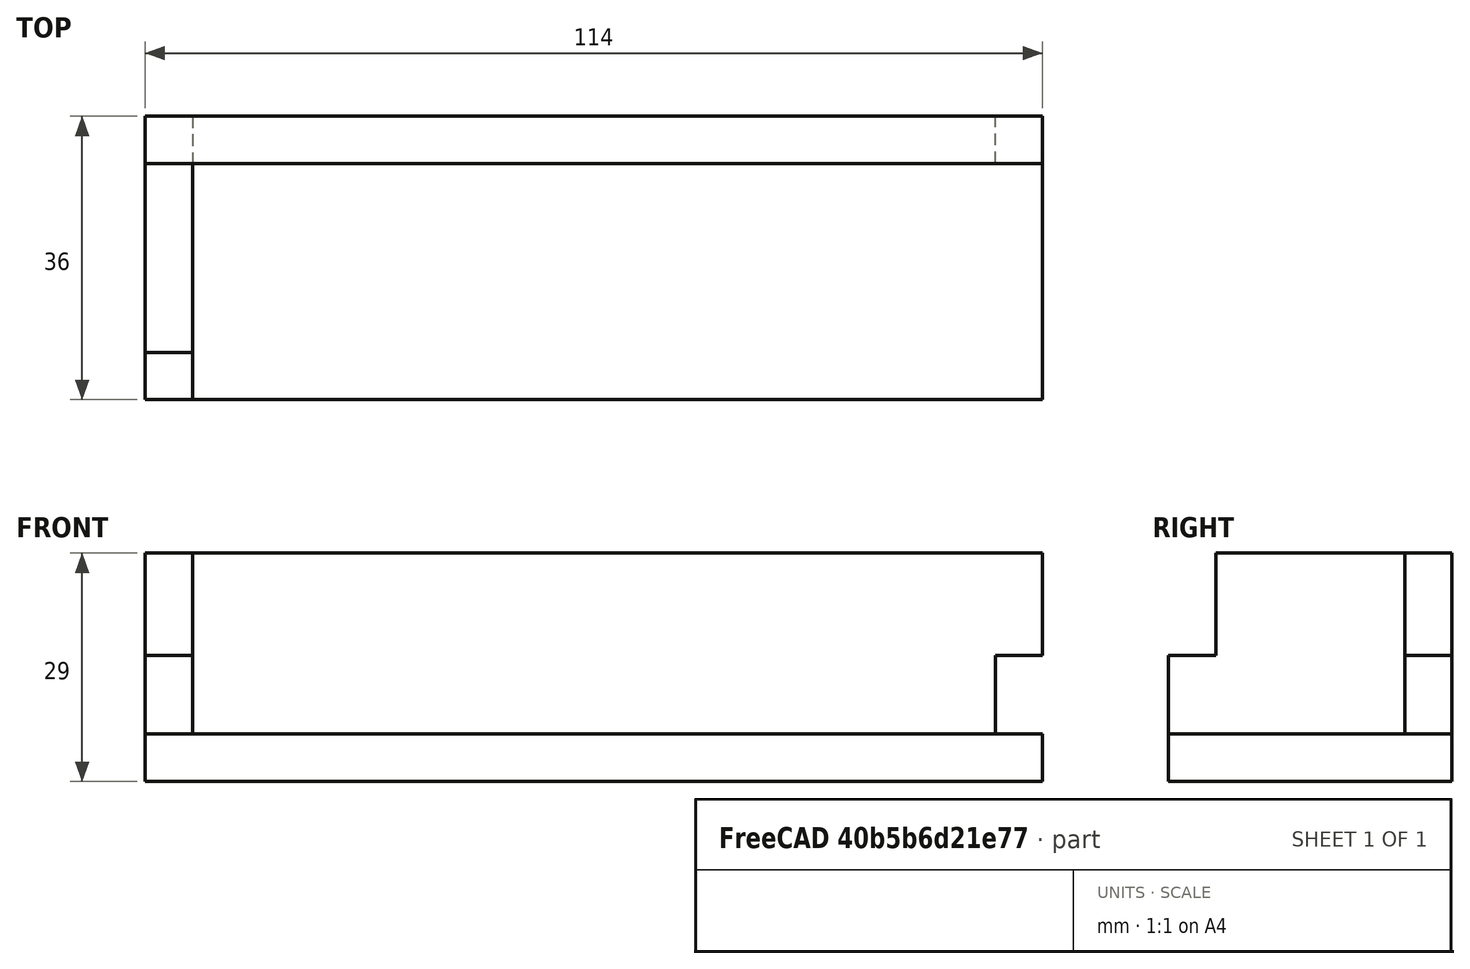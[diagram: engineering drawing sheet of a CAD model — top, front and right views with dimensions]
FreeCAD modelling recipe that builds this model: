
FCSTD DOCUMENT  (FreeCAD 0.18R16146 (Git))
Label: brass birmingham - resource tray
License: All rights reserved
LicenseURL: http://en.wikipedia.org/wiki/All_rights_reserved
objects: TechDraw::DrawViewPart×7, Sketcher::SketchObject×5, PartDesign::Body×5, PartDesign::Pad×3, Spreadsheet::Sheet×2, PartDesign::Pocket×2, PartDesign::FeatureBase×2, App::DocumentObjectGroup×2, TechDraw::DrawSVGTemplate×2, TechDraw::DrawViewDimension×2, TechDraw::DrawPage×2
note: 22 computed .brp shape members not serialized (recipe doc carries the construction recipe); baked Part::Feature solids carry a one-line shape summary decoded from their .brp

FEATURE [Spreadsheet::Sheet] Spreadsheet  label="my_variables"
  cells = A1=foam_width; B1(foam_width)==6mm; A2=lower_height; B2(lower_height)==29mm; A3=outer height (minus base); B3(height_adjusted)==38mm - B1; A4=outer long width; B4(width_long)==96mm; A5=outer short width; B5(width_short)==59mm
FEATURE [Sketcher::SketchObject] Sketch
  MapMode = 5
  Support = -> [XY_Plane]
  expr: Constraints[9] = my_variables001.width_short
  expr: Constraints[10] = my_variables001.width_long
  sketch-geometry (4):
    g0: LineSegment StartX=-57 StartY=36 StartZ=0 EndX=57 EndY=36 EndZ=0
    g1: LineSegment StartX=57 StartY=36 StartZ=0 EndX=57 EndY=0 EndZ=0
    g2: LineSegment StartX=57 StartY=0 StartZ=0 EndX=-57 EndY=0 EndZ=0
    g3: LineSegment StartX=-57 StartY=0 StartZ=0 EndX=-57 EndY=36 EndZ=0
  constraints (11):
    c: Coincident(g0,g1)
    c: Coincident(g1,g2)
    c: Coincident(g2,g3)
    c: Coincident(g3,g0)
    c: Horizontal(g0)
    c: Horizontal(g2)
    c: Vertical(g1)
    c: Vertical(g3)
    c: Symmetric(g2,g2,g-1)
    c: Distance(g3) = 36
    c: Distance(g2) = 114
FEATURE [PartDesign::Pad] Pad
  Length = 6
  Length2 = 100
  Profile = -> Sketch
  Type = 0
  expr: Length = my_variables.foam_width
FEATURE [PartDesign::Body] Body  label="base"
  Group = -> [Sketch,Pad]
  Origin = -> Origin
  Tip = -> Pad
FEATURE [Sketcher::SketchObject] Sketch001
  MapMode = 5
  Placement = pos=(0,0,0) rot=(1,0,0;1.5708rad)
  Support = -> [XZ_Plane001]
  expr: Constraints[10] = my_variables001.width_long
  expr: Constraints[9] = my_variables001.height_adjusted
  sketch-geometry (4):
    g0: LineSegment StartX=-57 StartY=23 StartZ=0 EndX=57 EndY=23 EndZ=0
    g1: LineSegment StartX=57 StartY=23 StartZ=0 EndX=57 EndY=0 EndZ=0
    g2: LineSegment StartX=57 StartY=0 StartZ=0 EndX=-57 EndY=0 EndZ=0
    g3: LineSegment StartX=-57 StartY=0 StartZ=0 EndX=-57 EndY=23 EndZ=0
  constraints (11):
    c: Coincident(g0,g1)
    c: Coincident(g1,g2)
    c: Coincident(g2,g3)
    c: Coincident(g3,g0)
    c: Horizontal(g0)
    c: Horizontal(g2)
    c: Vertical(g1)
    c: Vertical(g3)
    c: Symmetric(g2,g2,g-1)
    c: Distance(g3) = 23
    c: Distance(g0) = 114
FEATURE [PartDesign::Pad] Pad001
  Length = 6
  Length2 = 100
  Placement = pos=(0,0,0) rot=(1,0,0;1.5708rad)
  Profile = -> Sketch001
  Type = 0
  expr: Length = my_variables.foam_width
FEATURE [Sketcher::SketchObject] Sketch002
  MapMode = 5
  Placement = pos=(0,-6,-1.3e-15) rot=(1,0,0;1.5708rad)
  Support = -> [Pad001]
  expr: Constraints[30] = my_variables.foam_width
  expr: Constraints[29] = my_variables.foam_width
  expr: Constraints[10] = Sketch001.Constraints[10]
  expr: Constraints[9] = Sketch001.Constraints[9]
  sketch-geometry (12):
    g0: LineSegment [constr] StartX=-57 StartY=23 StartZ=0 EndX=57 EndY=23 EndZ=0
    g1: LineSegment [constr] StartX=57 StartY=23 StartZ=0 EndX=57 EndY=0 EndZ=0
    g2: LineSegment [constr] StartX=57 StartY=0 StartZ=0 EndX=-57 EndY=0 EndZ=0
    g3: LineSegment [constr] StartX=-57 StartY=0 StartZ=0 EndX=-57 EndY=23 EndZ=0
    g4: LineSegment StartX=-57 StartY=10 StartZ=0 EndX=-51 EndY=10 EndZ=0
    g5: LineSegment StartX=-51 StartY=10 StartZ=0 EndX=-51 EndY=0 EndZ=0
    g6: LineSegment StartX=-51 StartY=0 StartZ=0 EndX=-57 EndY=0 EndZ=0
    g7: LineSegment StartX=-57 StartY=0 StartZ=0 EndX=-57 EndY=10 EndZ=0
    g8: LineSegment StartX=51 StartY=10 StartZ=0 EndX=57 EndY=10 EndZ=0
    g9: LineSegment StartX=57 StartY=10 StartZ=0 EndX=57 EndY=0 EndZ=0
    g10: LineSegment StartX=57 StartY=0 StartZ=0 EndX=51 EndY=0 EndZ=0
    g11: LineSegment StartX=51 StartY=0 StartZ=0 EndX=51 EndY=10 EndZ=0
  constraints (33):
    c: Coincident(g0,g1)
    c: Coincident(g1,g2)
    c: Coincident(g2,g3)
    c: Coincident(g3,g0)
    c: Horizontal(g0)
    c: Horizontal(g2)
    c: Vertical(g1)
    c: Vertical(g3)
    c: Symmetric(g2,g2,g-1)
    c: Distance(g3) = 23
    c: Distance(g0) = 114
    c: Coincident(g4,g5)
    c: Coincident(g5,g6)
    c: Coincident(g6,g7)
    c: Coincident(g7,g4)
    c: Horizontal(g4)
    c: Horizontal(g6)
    c: Vertical(g5)
    c: Vertical(g7)
    c: Coincident(g8,g9)
    c: Coincident(g9,g10)
    c: Coincident(g10,g11)
    c: Coincident(g11,g8)
    c: Horizontal(g8)
    c: Horizontal(g10)
    c: Vertical(g9)
    c: Vertical(g11)
    c: Coincident(g6,g2)
    c: Coincident(g9,g1)
    c: Distance(g4) = 6
    c: Distance(g8) = 6
    c: Distance(g5) = 10
    c: Distance(g11) = 10
FEATURE [PartDesign::Pocket] Pocket
  BaseFeature = -> Pad001
  Length = 5
  Length2 = 100
  Placement = pos=(0,0,0) rot=(1,0,0;1.5708rad)
  Profile = -> Sketch002
  Type = 1
FEATURE [PartDesign::Body] Body001  label="side long"
  Group = -> [Sketch001,Pad001,Sketch002,Pocket]
  Origin = -> Origin001
  Placement = pos=(7e-15,6,6) rot=(0,0,1;0rad)
  Tip = -> Pocket
FEATURE [PartDesign::FeatureBase] Clone
  BaseFeature = -> Body001
  Placement = pos=(7e-15,6,6) rot=(0,0,1;0rad)
FEATURE [PartDesign::Body] Body002  label="side long - clone"
  BaseFeature = -> Body001
  Group = -> [Clone]
  Origin = -> Origin002
  Placement = pos=(-1.4e-14,30,-1.1e-14) rot=(0,0,1;0rad)
  Tip = -> Clone
FEATURE [Sketcher::SketchObject] Sketch003
  MapMode = 5
  Placement = pos=(0,0,0) rot=(0.57735,0.57735,0.57735;2.0944rad)
  Support = -> [YZ_Plane003]
  expr: Constraints[10] = my_variables001.width_short
  expr: Constraints[9] = my_variables001.height_adjusted
  sketch-geometry (4):
    g0: LineSegment StartX=-18 StartY=23 StartZ=0 EndX=18 EndY=23 EndZ=0
    g1: LineSegment StartX=18 StartY=23 StartZ=0 EndX=18 EndY=0 EndZ=0
    g2: LineSegment StartX=18 StartY=0 StartZ=0 EndX=-18 EndY=0 EndZ=0
    g3: LineSegment StartX=-18 StartY=0 StartZ=0 EndX=-18 EndY=23 EndZ=0
  constraints (11):
    c: Coincident(g0,g1)
    c: Coincident(g1,g2)
    c: Coincident(g2,g3)
    c: Coincident(g3,g0)
    c: Horizontal(g0)
    c: Horizontal(g2)
    c: Vertical(g1)
    c: Vertical(g3)
    c: Symmetric(g2,g2,g-1)
    c: Distance(g3) = 23
    c: Distance(g0) = 36
FEATURE [PartDesign::Pad] Pad002
  Length = 6
  Length2 = 100
  Placement = pos=(0,0,0) rot=(0.57735,0.57735,0.57735;2.0944rad)
  Profile = -> Sketch003
  Type = 0
  expr: Length = my_variables.foam_width
FEATURE [Sketcher::SketchObject] Sketch004
  MapMode = 5
  Placement = pos=(6,-2.7e-15,2e-15) rot=(0.57735,0.57735,0.57735;2.0944rad)
  Support = -> [Pad002]
  expr: Constraints[31] = my_variables001.foam_width
  expr: Constraints[20] = my_variables001.foam_width
  expr: Constraints[9] = Sketch003.Constraints[9]
  expr: Constraints[10] = Sketch003.Constraints[10]
  sketch-geometry (12):
    g0: LineSegment [constr] StartX=-18 StartY=23 StartZ=0 EndX=18 EndY=23 EndZ=0
    g1: LineSegment [constr] StartX=18 StartY=23 StartZ=0 EndX=18 EndY=0 EndZ=0
    g2: LineSegment [constr] StartX=18 StartY=0 StartZ=0 EndX=-18 EndY=0 EndZ=0
    g3: LineSegment [constr] StartX=-18 StartY=0 StartZ=0 EndX=-18 EndY=23 EndZ=0
    g4: LineSegment StartX=12 StartY=23 StartZ=0 EndX=18 EndY=23 EndZ=0
    g5: LineSegment StartX=18 StartY=23 StartZ=0 EndX=18 EndY=10 EndZ=0
    g6: LineSegment StartX=18 StartY=10 StartZ=0 EndX=12 EndY=10 EndZ=0
    g7: LineSegment StartX=12 StartY=10 StartZ=0 EndX=12 EndY=23 EndZ=0
    g8: LineSegment StartX=-12 StartY=10 StartZ=0 EndX=-18 EndY=10 EndZ=0
    g9: LineSegment StartX=-18 StartY=10 StartZ=0 EndX=-18 EndY=23 EndZ=0
    g10: LineSegment StartX=-18 StartY=23 StartZ=0 EndX=-12 EndY=23 EndZ=0
    g11: LineSegment StartX=-12 StartY=23 StartZ=0 EndX=-12 EndY=10 EndZ=0
  constraints (33):
    c: Coincident(g0,g1)
    c: Coincident(g1,g2)
    c: Coincident(g2,g3)
    c: Coincident(g3,g0)
    c: Horizontal(g0)
    c: Horizontal(g2)
    c: Vertical(g1)
    c: Vertical(g3)
    c: Symmetric(g2,g2,g-1)
    c: Distance(g3) = 23
    c: Distance(g0) = 36
    c: Coincident(g4,g5)
    c: Coincident(g5,g6)
    c: Coincident(g6,g7)
    c: Coincident(g7,g4)
    c: Horizontal(g4)
    c: Horizontal(g6)
    c: Vertical(g5)
    c: Vertical(g7)
    c: Coincident(g4,g0)
    c: Distance(g6) = 6
    c: Distance(g5,g1) = 10
    c: Coincident(g8,g9)
    c: Coincident(g9,g10)
    c: Coincident(g10,g11)
    c: Coincident(g11,g8)
    c: Horizontal(g8)
    c: Horizontal(g10)
    c: Vertical(g9)
    c: Vertical(g11)
    c: Coincident(g9,g0)
    c: Distance(g8) = 6
    c: Distance(g8,g2) = 10
FEATURE [PartDesign::Pocket] Pocket001
  BaseFeature = -> Pad002
  Length = 5
  Length2 = 100
  Placement = pos=(0,0,0) rot=(0.57735,0.57735,0.57735;2.0944rad)
  Profile = -> Sketch004
  Type = 1
FEATURE [PartDesign::Body] Body003  label="side short"
  Group = -> [Sketch003,Pad002,Sketch004,Pocket001]
  Origin = -> Origin003
  Placement = pos=(51,18,6) rot=(0,0,1;0rad)
  Tip = -> Pocket001
FEATURE [App::DocumentObjectGroup] Group  label="parts"
  Group = -> [Body,Body001,Body003]
FEATURE [PartDesign::FeatureBase] Clone001
  BaseFeature = -> Body003
  Placement = pos=(34,25,6) rot=(0,0,1;0rad)
FEATURE [PartDesign::Body] Body004  label="side small - clone"
  BaseFeature = -> Body003
  Group = -> [Clone001]
  Origin = -> Origin004
  Placement = pos=(-91,-7,-2e-16) rot=(0,0,1;0rad)
  Tip = -> Clone001
FEATURE [App::DocumentObjectGroup] Group001  label="clones"
  Group = -> [Body002,Body004]
FEATURE [TechDraw::DrawSVGTemplate] Template
  Height = 210
  Orientation = 1
  Width = 297
FEATURE [TechDraw::DrawViewPart] View002
  CoarseView = false
  Direction = (0,0,1)
  Focus = 100
  HardHidden = false
  IsoCount = 0
  IsoHidden = false
  IsoVisible = false
  LockPosition = false
  Perspective = false
  Rotation = 0
  ScaleType = 0
  SeamHidden = false
  SeamVisible = false
  SmoothHidden = false
  SmoothVisible = false
  Source = -> [Body]
  X = 62.9845
  Y = 172.655
FEATURE [TechDraw::DrawViewDimension] Dimension
  Arbitrary = false
  FormatSpec = %.2f
  LockPosition = false
  MeasureType = 1
  OverTolerance = 0
  References2D = -> [View002]
  Rotation = 0
  ScaleType = 0
  Type = 0
  UnderTolerance = 0
  X = -58.2835
  Y = 2.70619
FEATURE [TechDraw::DrawViewDimension] Dimension001
  Arbitrary = false
  FormatSpec = %.2f
  LockPosition = false
  MeasureType = 1
  OverTolerance = 0
  References2D = -> [View002]
  Rotation = 0
  ScaleType = 0
  Type = 0
  UnderTolerance = 0
  X = -4.05928
  Y = -40.5954
FEATURE [TechDraw::DrawViewPart] View003
  CoarseView = false
  Direction = (0,-1,0)
  Focus = 100
  HardHidden = false
  IsoCount = 0
  IsoHidden = false
  IsoVisible = false
  LockPosition = false
  Perspective = false
  Rotation = 0
  ScaleType = 0
  SeamHidden = false
  SeamVisible = false
  SmoothHidden = false
  SmoothVisible = false
  Source = -> [Body001]
  X = 63.2552
  Y = 99.0464
FEATURE [Spreadsheet::Sheet] Spreadsheet001  label="my_variables001"
  cells = A1=foam_width; B1(foam_width)==6mm; A3=outer height (minus base); B3(height_adjusted)==29mm - B1; A4=outer long width; B4(width_long)==114mm; A5=outer short width; B5(width_short)==36mm
FEATURE [TechDraw::DrawViewPart] View004
  CoarseView = false
  Direction = (0,-1,0)
  Focus = 100
  HardHidden = false
  IsoCount = 0
  IsoHidden = false
  IsoVisible = false
  LockPosition = false
  Perspective = false
  Rotation = 0
  ScaleType = 0
  SeamHidden = false
  SeamVisible = false
  SmoothHidden = false
  SmoothVisible = false
  Source = -> [Body001]
  X = 64.3376
  Y = 47.8995
FEATURE [TechDraw::DrawViewPart] View005
  CoarseView = false
  Direction = (1,0,0)
  Focus = 100
  HardHidden = false
  IsoCount = 0
  IsoHidden = false
  IsoVisible = false
  LockPosition = false
  Perspective = false
  Rotation = 0
  ScaleType = 0
  SeamHidden = false
  SeamVisible = false
  SmoothHidden = false
  SmoothVisible = false
  Source = -> [Body003]
  X = 188.822
  Y = 186.997
FEATURE [TechDraw::DrawViewPart] View006
  CoarseView = false
  Direction = (1,0,0)
  Focus = 100
  HardHidden = false
  IsoCount = 0
  IsoHidden = false
  IsoVisible = false
  LockPosition = false
  Perspective = false
  Rotation = 0
  ScaleType = 0
  SeamHidden = false
  SeamVisible = false
  SmoothHidden = false
  SmoothVisible = false
  Source = -> [Body003]
  X = 188.01
  Y = 141.534
FEATURE [TechDraw::DrawSVGTemplate] Template001
  Height = 210
  Orientation = 1
  Width = 297
FEATURE [TechDraw::DrawViewPart] View
  CoarseView = false
  Direction = (0.577,-0.577,0.577)
  Focus = 100
  HardHidden = false
  IsoCount = 0
  IsoHidden = false
  IsoVisible = false
  LockPosition = false
  Perspective = false
  Rotation = 0
  Scale = 1.5
  ScaleType = 0
  SeamHidden = false
  SeamVisible = false
  SmoothHidden = false
  SmoothVisible = false
  Source = -> [Body,Body004,Body003,Body002,Body001,Group001]
  X = 149.853
  Y = 105.812
FEATURE [TechDraw::DrawPage] Page001  label="iso view"
  KeepUpdated = true
  ProjectionType = 0
  Scale = 1.5
  Template = -> Template001
  Views = -> [View]
FEATURE [TechDraw::DrawViewPart] View007
  CoarseView = false
  Direction = (0,0,1)
  Focus = 100
  HardHidden = false
  IsoCount = 0
  IsoHidden = false
  IsoVisible = false
  LockPosition = false
  Perspective = false
  Rotation = 0
  ScaleType = 0
  SeamHidden = false
  SeamVisible = false
  SmoothHidden = false
  SmoothVisible = false
  Source = -> [Body,Body004,Body003,Body002,Body001,Group001]
  X = 202.353
  Y = 83.0799
FEATURE [TechDraw::DrawPage] Page  label="Parts"
  KeepUpdated = true
  ProjectionType = 0
  Template = -> Template
  Views = -> [View002,Dimension,Dimension001,View003,View004,View005,View006,View007]
